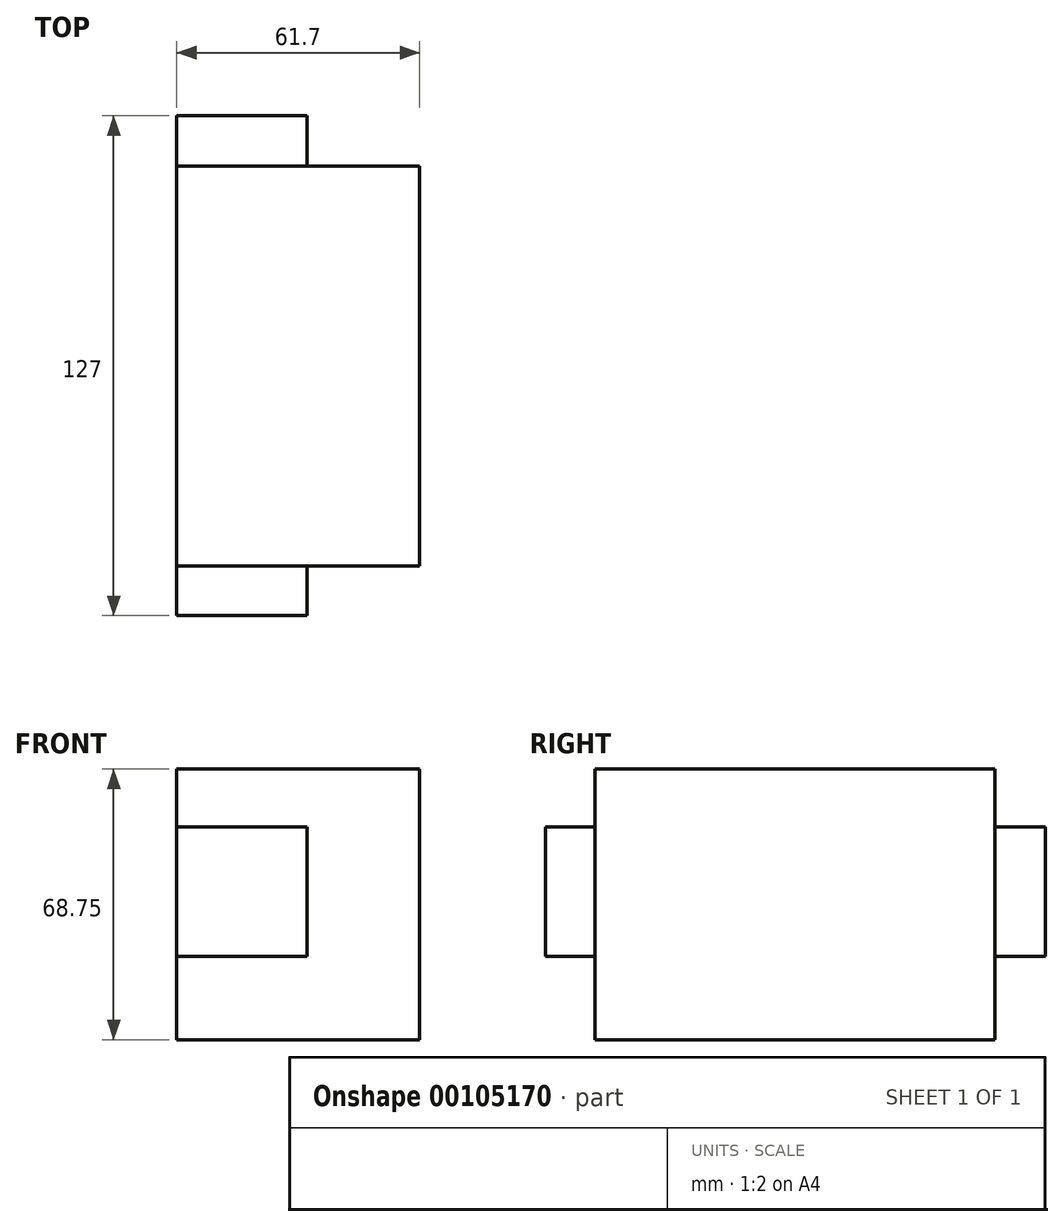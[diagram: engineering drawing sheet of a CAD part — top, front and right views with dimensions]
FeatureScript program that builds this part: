
annotation { "Feature Type Name" : "Feature", "Feature Type Description" : "" }
export const myFeature = defineFeature(function(context is Context, id is Id, definition is map)
    precondition{}
    {
        {
            var Q0;
            Q0=qCreatedBy(makeId("Front.planeOp"),FACE);
            var sketch = newSketch(context, id + "F0", { "sketchPlane" : qUnion([Q0])});
            skLineSegment(sketch, "E0.bottom", {"start": v(-33.1, 35.16) * mm, "end": v(28.6, 35.16) * mm});
            skLineSegment(sketch, "E0.top", {"start": v(-33.1, -33.6) * mm, "end": v(28.6, -33.6) * mm});
            skLineSegment(sketch, "E0.left", {"start": v(-33.1, 35.16) * mm, "end": v(-33.1, -33.6) * mm});
            skLineSegment(sketch, "E0.right", {"start": v(28.6, 35.16) * mm, "end": v(28.6, -33.6) * mm});
            skSolve(sketch);
        }
        {
            var Q0;
            Q0=makeQuery(id+"F0.imprint","IMPRINT",FACE,{"disambiguationData":[TD([[makeQuery(id+"F0.imprint","IMPRINT",EDGE,{"derivedFrom":sQuery(id+"F0.wireOp",EDGE,"E0.bottom")}),-1.0]])]});
            extrude(context, id + "F1", {"entities" : qUnion([Q0]), "depth" : 50.8 * mm});
        }
        {
            var Q0;
            Q0=makeQuery(id+"F1.opExtrude","CAP_FACE",FACE,{"disambiguationData":[OSD([sQuery(id+"F0.wireOp",EDGE,"E0.bottom"),sQuery(id+"F0.wireOp",EDGE,"E0.top"),sQuery(id+"F0.wireOp",EDGE,"E0.left"),sQuery(id+"F0.wireOp",EDGE,"E0.right")])],"isStart":false});
            var Q1;
            Q1=makeQuery(id+"F1.opExtrude","CAP_FACE",FACE,{"disambiguationData":[OSD([sQuery(id+"F0.wireOp",EDGE,"E0.bottom"),sQuery(id+"F0.wireOp",EDGE,"E0.top"),sQuery(id+"F0.wireOp",EDGE,"E0.left"),sQuery(id+"F0.wireOp",EDGE,"E0.right")])],"isStart":true});
            extrude(context, id + "F2", {"entities" : qUnion([Q0, Q1]), "operationType" : NewBodyOperationType.ADD, "depth" : 25.4 * mm});
        }
        {
            var Q0;
            {var subQ0=sQuery(id+"F0.wireOp",EDGE,"E0.right");var subQ1=sQuery(id+"F0.wireOp",EDGE,"E0.left");var subQ2=sQuery(id+"F0.wireOp",EDGE,"E0.top");var subQ3=sQuery(id+"F0.wireOp",EDGE,"E0.bottom");Q0=makeQuery(id+"F2.opExtrude","CAP_FACE",FACE,{"disambiguationData":[OSD([subQ3,subQ2,subQ1,subQ0]),TDD([makeQuery(id+"F1.opExtrude","CAP_FACE",FACE,{"disambiguationData":[OSD([subQ3,subQ2,subQ1,subQ0])],"isStart":false})])],"isStart":false});}
            extrude(context, id + "F3", {"entities" : qUnion([Q0]), "operationType" : NewBodyOperationType.ADD, "depth" : 25.4 * mm});
        }
        {
            var Q0;
            Q0=makeQuery(id+"F3.opExtrude","CAP_FACE",FACE,{"disambiguationData":[OSD([sQuery(id+"F0.wireOp",EDGE,"E0.bottom"),sQuery(id+"F0.wireOp",EDGE,"E0.top"),sQuery(id+"F0.wireOp",EDGE,"E0.left"),sQuery(id+"F0.wireOp",EDGE,"E0.right")])],"isStart":false});
            var sketch = newSketch(context, id + "F4", { "sketchPlane" : qUnion([Q0])});
            skSolve(sketch);
        }
        {
            var Q0;
            Q0=makeQuery(id+"F4.imprint","IMPRINT",FACE,{"disambiguationData":[TD([[makeQuery(id+"F4.imprint","IMPRINT",EDGE,{"derivedFrom":makeQuery(id+"F3.opExtrude","CAP_EDGE",EDGE,{"disambiguationData":[OSD([sQuery(id+"F0.wireOp",EDGE,"E0.bottom")])],"isStart":false})}),-1.0]])]});
            var sketch = newSketch(context, id + "F5", { "sketchPlane" : qUnion([Q0])});
            skLineSegment(sketch, "E1", {"start": v(-33.1, 20.47) * mm, "end": v(0, 20.47) * mm});
            skLineSegment(sketch, "E2", {"start": v(0, 20.47) * mm, "end": v(0, -12.44) * mm});
            skLineSegment(sketch, "E3", {"start": v(0, -12.44) * mm, "end": v(-33.69, -12.44) * mm});
            skSolve(sketch);
        }
        {
            var Q0;
            {var subQ0=sQuery(id+"F5.wireOp",EDGE,"E1");Q0=makeQuery(id+"F5.imprint","IMPRINT",FACE,{"disambiguationData":[TD([[makeQuery(id+"F5.imprint","IMPRINT",EDGE,{"derivedFrom":subQ0}),-1.0]])]});}
            extrude(context, id + "F6", {"entities" : qUnion([Q0]), "operationType" : NewBodyOperationType.ADD, "oppositeDirection" : true, "depth" : 114.4 * mm});
        }
        {
            var Q0;
            Q0=makeQuery(id+"F6.opExtrude","CAP_FACE",FACE,{"disambiguationData":[OSD([sQuery(id+"F0.wireOp",EDGE,"E0.left"),sQuery(id+"F5.wireOp",EDGE,"E1"),sQuery(id+"F5.wireOp",EDGE,"E2"),sQuery(id+"F5.wireOp",EDGE,"E3")])],"isStart":false});
            extrude(context, id + "F7", {"entities" : qUnion([Q0]), "operationType" : NewBodyOperationType.ADD, "oppositeDirection" : true, "depth" : 76.93 * mm});
        }
        {
            var Q0;
            Q0=makeQuery(id+"F6.opExtrude","CAP_FACE",FACE,{"disambiguationData":[OSD([sQuery(id+"F0.wireOp",EDGE,"E0.left"),sQuery(id+"F5.wireOp",EDGE,"E1"),sQuery(id+"F5.wireOp",EDGE,"E2"),sQuery(id+"F5.wireOp",EDGE,"E3")])],"isStart":false});
            extrude(context, id + "F8", {"entities" : qUnion([Q0]), "operationType" : NewBodyOperationType.ADD, "oppositeDirection" : true, "depth" : 127 * mm});
        }
        {
            var Q0;
            Q0=makeQuery(id+"F8.opExtrude","CAP_FACE",FACE,{"disambiguationData":[OSD([sQuery(id+"F0.wireOp",EDGE,"E0.left"),sQuery(id+"F5.wireOp",EDGE,"E1"),sQuery(id+"F5.wireOp",EDGE,"E2"),sQuery(id+"F5.wireOp",EDGE,"E3")])],"isStart":false});
            extrude(context, id + "F9", {"entities" : qUnion([Q0]), "operationType" : NewBodyOperationType.ADD, "oppositeDirection" : true, "depth" : 80.69 * mm});
        }
    });
